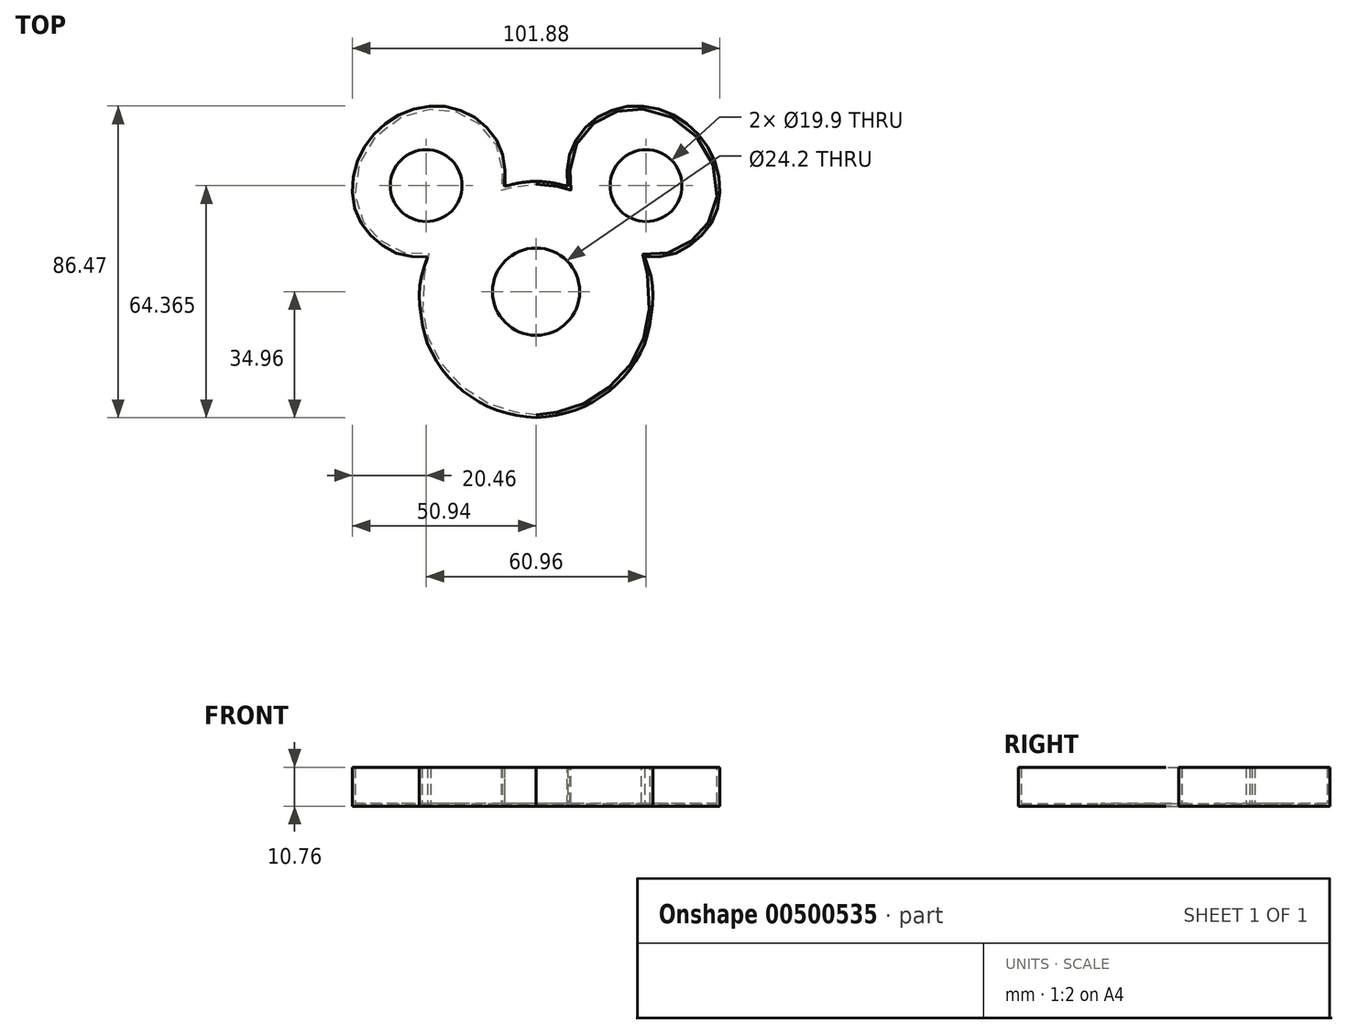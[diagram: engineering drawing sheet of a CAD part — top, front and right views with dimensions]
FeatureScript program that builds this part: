
annotation { "Feature Type Name" : "Feature", "Feature Type Description" : "" }
export const myFeature = defineFeature(function(context is Context, id is Id, definition is map)
    precondition{}
    {
        {
            var Q0;
            Q0=qCreatedBy(makeId("Top.planeOp"),FACE);
            var sketch = newSketch(context, id + "F0", { "sketchPlane" : qUnion([Q0])});
            skFitSpline(sketch, "E0", {"points": [v(0, -34.2) * mm, v(-3.72, -33.84) * mm, v(-10.52, -32.21) * mm, v(-17.7, -28.49) * mm, v(-24.37, -22.46) * mm, v(-29.21, -14.5) * mm, v(-30.97, -7.69) * mm, v(-31.1, 4.07) * mm, v(-29.26, 10.22) * mm, v(-30.19, 10.37) * mm, v(-37.35, 10.97) * mm, v(-42.86, 13.92) * mm, v(-47.1, 18.22) * mm, v(-49.83, 24.5) * mm, v(-49.42, 33.95) * mm, v(-44.56, 42.99) * mm, v(-36.93, 48.69) * mm, v(-28.75, 50.72) * mm, v(-22.5, 50) * mm, v(-16.69, 47.2) * mm, v(-11.75, 41.83) * mm, v(-9.6, 35.9) * mm, v(-9.55, 28.96) * mm, v(-9.67, 28.23) * mm, v(-9.4, 28.23) * mm, v(-7.7, 28.67) * mm, v(-4.72, 29.38) * mm, v(0, 29.87) * mm], "startDerivative": vector(-115.76, 6.66) * mm, "endDerivative": vector(134.87, 7.87) * mm});
            skFitSpline(sketch, "E1.MirrorCS", {"points": [v(0, -34.2) * mm, v(3.72, -33.84) * mm, v(10.52, -32.21) * mm, v(17.7, -28.49) * mm, v(24.37, -22.46) * mm, v(29.21, -14.5) * mm, v(30.97, -7.69) * mm, v(31.1, 4.07) * mm, v(29.26, 10.22) * mm, v(30.19, 10.37) * mm, v(37.35, 10.97) * mm, v(42.86, 13.92) * mm, v(47.1, 18.22) * mm, v(49.83, 24.5) * mm, v(49.42, 33.95) * mm, v(44.56, 42.99) * mm, v(36.93, 48.69) * mm, v(28.75, 50.72) * mm, v(22.5, 50) * mm, v(16.69, 47.2) * mm, v(11.75, 41.83) * mm, v(9.6, 35.9) * mm, v(9.55, 28.96) * mm, v(9.67, 28.23) * mm, v(9.4, 28.23) * mm, v(7.7, 28.67) * mm, v(4.72, 29.38) * mm, v(0, 29.87) * mm], "startDerivative": vector(115.76, 6.66) * mm, "endDerivative": vector(-134.87, 7.87) * mm});
            skSolve(sketch);
        }
        {
            var Q0;
            Q0=makeQuery(id+"F0.imprint","IMPRINT",FACE,{"disambiguationData":[TD([[makeQuery(id+"F0.imprint","IMPRINT",EDGE,{"derivedFrom":sQuery(id+"F0.wireOp",EDGE,"E0")}),-1.0]])]});
            extrude(context, id + "F1", {"entities" : qUnion([Q0]), "depth" : 10 * mm});
        }
        {
            var Q0;
            Q0=makeQuery(id+"F1.opExtrude","CAP_FACE",FACE,{"disambiguationData":[OSD([sQuery(id+"F0.wireOp",EDGE,"E0"),sQuery(id+"F0.wireOp",EDGE,"E1.MirrorCS")])],"isStart":false});
            shell(context, id + "F2", {"entities" : qUnion([Q0]), "thickness" : 0.76 * mm, "oppositeDirection" : true});
        }
        {
            var Q0;
            Q0=qCreatedBy(makeId("Top.planeOp"),FACE);
            var sketch = newSketch(context, id + "F3", { "sketchPlane" : qUnion([Q0])});
            skCircle(sketch, "E2", {"center": v(0, 0) * mm, "radius": 12.1 * mm});
            skCircle(sketch, "E3", {"center": v(-30.48, 29.4) * mm, "radius": 9.95 * mm});
            skCircle(sketch, "E4.MirrorC", {"center": v(30.48, 29.4) * mm, "radius": 9.95 * mm});
            skSolve(sketch);
        }
        {
            var Q0;
            Q0 = qSketchRegion(id + "F3", true);
            extrude(context, id + "F4", {"entities" : qUnion([Q0]), "operationType" : NewBodyOperationType.REMOVE, "oppositeDirection" : true, "depth" : 8.64 * mm});
        }
    });
